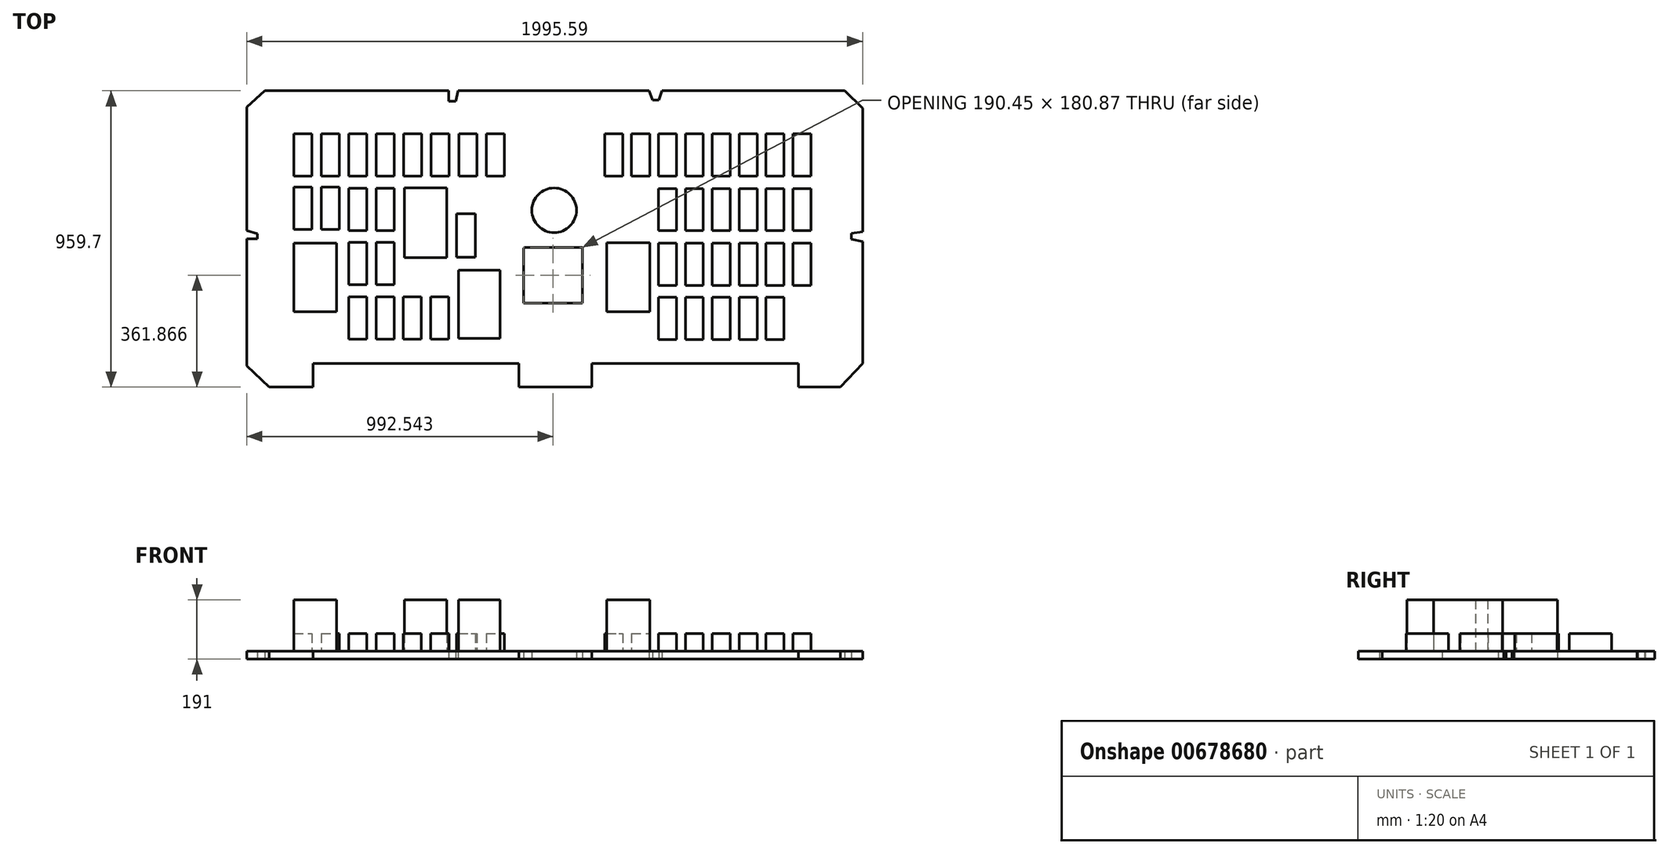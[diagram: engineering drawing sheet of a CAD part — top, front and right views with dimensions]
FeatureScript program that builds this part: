
annotation { "Feature Type Name" : "Feature", "Feature Type Description" : "" }
export const myFeature = defineFeature(function(context is Context, id is Id, definition is map)
    precondition{}
    {
        {
            var Q0;
            Q0=qCreatedBy(makeId("Top.planeOp"),FACE);
            var sketch = newSketch(context, id + "F0", { "sketchPlane" : qUnion([Q0])});
            skLineSegment(sketch, "E0.bottom", {"start": v(-887.12, 318.46) * mm, "end": v(-290.84, 318.46) * mm});
            skLineSegment(sketch, "E0.top", {"start": v(-872.01, -641.24) * mm, "end": v(-729.99, -641.24) * mm});
            skLineSegment(sketch, "E0.left", {"start": v(-945.57, 265.32) * mm, "end": v(-945.57, -134.43) * mm});
            skLineSegment(sketch, "E0.right", {"start": v(1050.02, 261.3) * mm, "end": v(1050.02, -138.6) * mm});
            skLineSegment(sketch, "E1.bottom", {"start": v(-792.44, 178.7) * mm, "end": v(-734.02, 178.7) * mm});
            skLineSegment(sketch, "E1.top", {"start": v(-792.44, 41.72) * mm, "end": v(-734.02, 41.72) * mm});
            skLineSegment(sketch, "E1.left", {"start": v(-792.44, 178.7) * mm, "end": v(-792.44, 41.72) * mm});
            skLineSegment(sketch, "E1.right", {"start": v(-734.02, 178.7) * mm, "end": v(-734.02, 41.72) * mm});
            skLineSegment(sketch, "E2.1.0.0", {"start": v(-703.44, 178.7) * mm, "end": v(-645.02, 178.7) * mm});
            skLineSegment(sketch, "E2.1.0.1", {"start": v(-703.44, 41.72) * mm, "end": v(-645.02, 41.72) * mm});
            skLineSegment(sketch, "E2.1.0.2", {"start": v(-703.44, 178.7) * mm, "end": v(-703.44, 41.72) * mm});
            skLineSegment(sketch, "E2.1.0.3", {"start": v(-645.02, 178.7) * mm, "end": v(-645.02, 41.72) * mm});
            skLineSegment(sketch, "E2.2.0.0", {"start": v(-614.44, 178.7) * mm, "end": v(-556.02, 178.7) * mm});
            skLineSegment(sketch, "E2.2.0.1", {"start": v(-614.44, 41.72) * mm, "end": v(-556.02, 41.72) * mm});
            skLineSegment(sketch, "E2.2.0.2", {"start": v(-614.44, 178.7) * mm, "end": v(-614.44, 41.72) * mm});
            skLineSegment(sketch, "E2.2.0.3", {"start": v(-556.02, 178.7) * mm, "end": v(-556.02, 41.72) * mm});
            skLineSegment(sketch, "E2.3.0.0", {"start": v(-525.44, 178.7) * mm, "end": v(-467.02, 178.7) * mm});
            skLineSegment(sketch, "E2.3.0.1", {"start": v(-525.44, 41.72) * mm, "end": v(-467.02, 41.72) * mm});
            skLineSegment(sketch, "E2.3.0.2", {"start": v(-525.44, 178.7) * mm, "end": v(-525.44, 41.72) * mm});
            skLineSegment(sketch, "E2.3.0.3", {"start": v(-467.02, 178.7) * mm, "end": v(-467.02, 41.72) * mm});
            skLineSegment(sketch, "E2.4.0.0", {"start": v(-436.44, 178.7) * mm, "end": v(-378.02, 178.7) * mm});
            skLineSegment(sketch, "E2.4.0.1", {"start": v(-436.44, 41.72) * mm, "end": v(-378.02, 41.72) * mm});
            skLineSegment(sketch, "E2.4.0.2", {"start": v(-436.44, 178.7) * mm, "end": v(-436.44, 41.72) * mm});
            skLineSegment(sketch, "E2.4.0.3", {"start": v(-378.02, 178.7) * mm, "end": v(-378.02, 41.72) * mm});
            skLineSegment(sketch, "E2.5.0.0", {"start": v(-347.44, 178.7) * mm, "end": v(-289.02, 178.7) * mm});
            skLineSegment(sketch, "E2.5.0.1", {"start": v(-347.44, 41.72) * mm, "end": v(-289.02, 41.72) * mm});
            skLineSegment(sketch, "E2.5.0.2", {"start": v(-347.44, 178.7) * mm, "end": v(-347.44, 41.72) * mm});
            skLineSegment(sketch, "E2.5.0.3", {"start": v(-289.02, 178.7) * mm, "end": v(-289.02, 41.72) * mm});
            skLineSegment(sketch, "E2.6.0.0", {"start": v(-258.44, 178.7) * mm, "end": v(-200.02, 178.7) * mm});
            skLineSegment(sketch, "E2.6.0.1", {"start": v(-258.44, 41.72) * mm, "end": v(-200.02, 41.72) * mm});
            skLineSegment(sketch, "E2.6.0.2", {"start": v(-258.44, 178.7) * mm, "end": v(-258.44, 41.72) * mm});
            skLineSegment(sketch, "E2.6.0.3", {"start": v(-200.02, 178.7) * mm, "end": v(-200.02, 41.72) * mm});
            skLineSegment(sketch, "E2.7.0.0", {"start": v(-169.44, 178.7) * mm, "end": v(-111.02, 178.7) * mm});
            skLineSegment(sketch, "E2.7.0.1", {"start": v(-169.44, 41.72) * mm, "end": v(-111.02, 41.72) * mm});
            skLineSegment(sketch, "E2.7.0.2", {"start": v(-169.44, 178.7) * mm, "end": v(-169.44, 41.72) * mm});
            skLineSegment(sketch, "E2.7.0.3", {"start": v(-111.02, 178.7) * mm, "end": v(-111.02, 41.72) * mm});
            skLineSegment(sketch, "E2.direction1", {"start": v(-792.44, 41.72) * mm, "end": v(-703.44, 41.72) * mm, "construction": true});
            skPoint(sketch, "E3", {"position": v(-945.57, 265.32) * mm});
            skPoint(sketch, "E4", {"position": v(-887.12, 318.46) * mm});
            skPoint(sketch, "E5", {"position": v(-290.84, 318.46) * mm});
            skPoint(sketch, "E6", {"position": v(-260.62, 318.46) * mm});
            skPoint(sketch, "E7", {"position": v(357.82, 318.46) * mm});
            skPoint(sketch, "E8", {"position": v(400.12, 318.46) * mm});
            skPoint(sketch, "E9", {"position": v(992.37, 318.46) * mm});
            skPoint(sketch, "E10", {"position": v(1050.02, 261.3) * mm});
            skPoint(sketch, "E11", {"position": v(1050.02, -564.63) * mm});
            skPoint(sketch, "E12", {"position": v(978.27, -641.24) * mm});
            skPoint(sketch, "E13", {"position": v(841.29, -641.24) * mm});
            skPoint(sketch, "E14", {"position": v(172.49, -641.24) * mm});
            skPoint(sketch, "E15", {"position": v(-63.2, -641.24) * mm});
            skPoint(sketch, "E16", {"position": v(-729.99, -641.24) * mm});
            skLineSegment(sketch, "E17", {"start": v(-945.57, 265.32) * mm, "end": v(-887.12, 318.46) * mm});
            skLineSegment(sketch, "E18", {"start": v(-290.84, 318.46) * mm, "end": v(-290.84, 284.99) * mm});
            skLineSegment(sketch, "E19", {"start": v(-290.84, 284.99) * mm, "end": v(-268.29, 284.99) * mm});
            skLineSegment(sketch, "E20", {"start": v(-268.29, 284.99) * mm, "end": v(-260.62, 318.46) * mm});
            skLineSegment(sketch, "E21", {"start": v(357.82, 318.46) * mm, "end": v(369.4, 287.8) * mm});
            skLineSegment(sketch, "E22", {"start": v(369.4, 287.8) * mm, "end": v(389.55, 287.8) * mm});
            skLineSegment(sketch, "E23", {"start": v(389.55, 287.8) * mm, "end": v(400.12, 318.46) * mm});
            skLineSegment(sketch, "E24", {"start": v(992.37, 318.46) * mm, "end": v(1050.02, 261.3) * mm});
            skLineSegment(sketch, "E25", {"start": v(1050.02, -564.63) * mm, "end": v(978.27, -641.24) * mm});
            skLineSegment(sketch, "E26", {"start": v(841.29, -641.24) * mm, "end": v(841.29, -564.63) * mm});
            skLineSegment(sketch, "E27", {"start": v(841.29, -564.63) * mm, "end": v(172.49, -564.63) * mm});
            skLineSegment(sketch, "E28", {"start": v(172.49, -564.63) * mm, "end": v(172.49, -641.24) * mm});
            skLineSegment(sketch, "E29", {"start": v(-63.2, -641.24) * mm, "end": v(-63.2, -564.63) * mm});
            skLineSegment(sketch, "E30", {"start": v(-63.2, -564.63) * mm, "end": v(-729.99, -564.63) * mm});
            skLineSegment(sketch, "E31", {"start": v(-729.99, -564.63) * mm, "end": v(-729.99, -641.24) * mm});
            skPoint(sketch, "E32", {"position": v(-872.01, -641.24) * mm});
            skPoint(sketch, "E33", {"position": v(-945.57, -572.57) * mm});
            skPoint(sketch, "E34", {"position": v(-945.57, -161.39) * mm});
            skPoint(sketch, "E35", {"position": v(-945.57, -134.43) * mm});
            skLineSegment(sketch, "E36", {"start": v(-945.57, -134.43) * mm, "end": v(-910.29, -144.5) * mm});
            skLineSegment(sketch, "E37", {"start": v(-910.29, -144.5) * mm, "end": v(-910.29, -161.62) * mm});
            skLineSegment(sketch, "E38", {"start": v(-910.29, -161.62) * mm, "end": v(-945.57, -161.39) * mm});
            skLineSegment(sketch, "E39", {"start": v(-945.57, -572.57) * mm, "end": v(-872.01, -641.24) * mm});
            skPoint(sketch, "E40.orphan", {"position": v(-945.57, -641.24) * mm});
            skLineSegment(sketch, "E41.trimOffspring", {"start": v(-63.2, -641.24) * mm, "end": v(172.49, -641.24) * mm});
            skLineSegment(sketch, "E42.trimOffspring", {"start": v(841.29, -641.24) * mm, "end": v(978.27, -641.24) * mm});
            skLineSegment(sketch, "E43", {"start": v(1050.02, -138.6) * mm, "end": v(1013.26, -143.68) * mm});
            skLineSegment(sketch, "E44", {"start": v(1013.26, -143.68) * mm, "end": v(1013.26, -163.16) * mm});
            skLineSegment(sketch, "E45", {"start": v(1013.26, -163.16) * mm, "end": v(1050.02, -170.78) * mm});
            skLineSegment(sketch, "E46.trimOffspring", {"start": v(1050.02, -170.78) * mm, "end": v(1050.02, -564.63) * mm});
            skLineSegment(sketch, "E47.trimOffspring", {"start": v(-945.57, -161.39) * mm, "end": v(-945.57, -572.57) * mm});
            skPoint(sketch, "E48.orphan", {"position": v(-945.57, 318.46) * mm});
            skLineSegment(sketch, "E49.trimOffspring", {"start": v(-260.62, 318.46) * mm, "end": v(357.82, 318.46) * mm});
            skLineSegment(sketch, "E50.trimOffspring", {"start": v(400.12, 318.46) * mm, "end": v(992.37, 318.46) * mm});
            skLineSegment(sketch, "E51.0.1.0", {"start": v(-792.44, 6.7) * mm, "end": v(-792.44, -130.28) * mm});
            skLineSegment(sketch, "E51.0.1.1", {"start": v(-703.44, 6.7) * mm, "end": v(-645.02, 6.7) * mm});
            skLineSegment(sketch, "E51.0.1.2", {"start": v(-792.44, -130.28) * mm, "end": v(-734.02, -130.28) * mm});
            skLineSegment(sketch, "E51.0.1.4", {"start": v(-792.44, 6.7) * mm, "end": v(-734.02, 6.7) * mm});
            skLineSegment(sketch, "E51.0.1.5", {"start": v(-734.02, 6.7) * mm, "end": v(-734.02, -130.28) * mm});
            skLineSegment(sketch, "E51.0.1.10", {"start": v(-703.44, -130.28) * mm, "end": v(-645.02, -130.28) * mm});
            skLineSegment(sketch, "E51.0.1.11", {"start": v(-645.02, 6.7) * mm, "end": v(-645.02, -130.28) * mm});
            skLineSegment(sketch, "E51.0.1.12", {"start": v(-703.44, 6.7) * mm, "end": v(-703.44, -130.28) * mm});
            skLineSegment(sketch, "E51.0.1.16", {"start": v(-792.44, -130.28) * mm, "end": v(-703.44, -130.28) * mm, "construction": true});
            skLineSegment(sketch, "E51.direction1", {"start": v(-792.44, 41.72) * mm, "end": v(-767.44, 41.72) * mm, "construction": true});
            skLineSegment(sketch, "E51.direction2", {"start": v(-792.44, 41.72) * mm, "end": v(-792.44, -130.28) * mm, "construction": true});
            skLineSegment(sketch, "E52.bottom", {"start": v(-434.49, 3.44) * mm, "end": v(-297.5, 3.44) * mm});
            skLineSegment(sketch, "E52.top", {"start": v(-434.49, -222.18) * mm, "end": v(-297.5, -222.18) * mm});
            skLineSegment(sketch, "E52.left", {"start": v(-434.49, 3.44) * mm, "end": v(-434.49, -222.18) * mm});
            skLineSegment(sketch, "E52.right", {"start": v(-297.5, 3.44) * mm, "end": v(-297.5, -222.18) * mm});
            skLineSegment(sketch, "E53.bottom", {"start": v(-793.06, -175.84) * mm, "end": v(-654.06, -175.84) * mm});
            skLineSegment(sketch, "E53.top", {"start": v(-793.06, -397.43) * mm, "end": v(-654.06, -397.43) * mm});
            skLineSegment(sketch, "E53.left", {"start": v(-793.06, -175.84) * mm, "end": v(-793.06, -397.43) * mm});
            skLineSegment(sketch, "E53.right", {"start": v(-654.06, -175.84) * mm, "end": v(-654.06, -397.43) * mm});
            skLineSegment(sketch, "E54.bottom", {"start": v(-259.23, -262.47) * mm, "end": v(-124.26, -262.47) * mm});
            skLineSegment(sketch, "E54.top", {"start": v(-259.23, -484.06) * mm, "end": v(-124.26, -484.06) * mm});
            skLineSegment(sketch, "E54.left", {"start": v(-259.23, -262.47) * mm, "end": v(-259.23, -484.06) * mm});
            skLineSegment(sketch, "E54.right", {"start": v(-124.26, -262.47) * mm, "end": v(-124.26, -484.06) * mm});
            skLineSegment(sketch, "E55.0.1.0", {"start": v(-525.44, -134.28) * mm, "end": v(-467.02, -134.28) * mm});
            skLineSegment(sketch, "E55.0.1.1", {"start": v(-525.44, 2.7) * mm, "end": v(-525.44, -134.28) * mm});
            skLineSegment(sketch, "E55.0.1.2", {"start": v(-525.44, 2.7) * mm, "end": v(-467.02, 2.7) * mm});
            skLineSegment(sketch, "E55.0.1.3", {"start": v(-614.44, -134.28) * mm, "end": v(-556.02, -134.28) * mm});
            skLineSegment(sketch, "E55.0.1.4", {"start": v(-467.02, 2.7) * mm, "end": v(-467.02, -134.28) * mm});
            skLineSegment(sketch, "E55.0.1.5", {"start": v(-556.02, 2.7) * mm, "end": v(-556.02, -134.28) * mm});
            skLineSegment(sketch, "E55.0.1.6", {"start": v(-614.44, 2.7) * mm, "end": v(-556.02, 2.7) * mm});
            skLineSegment(sketch, "E55.0.1.7", {"start": v(-614.44, 2.7) * mm, "end": v(-614.44, -134.28) * mm});
            skLineSegment(sketch, "E55.0.2.0", {"start": v(-525.44, -310.28) * mm, "end": v(-467.02, -310.28) * mm});
            skLineSegment(sketch, "E55.0.2.1", {"start": v(-525.44, -173.3) * mm, "end": v(-525.44, -310.28) * mm});
            skLineSegment(sketch, "E55.0.2.2", {"start": v(-525.44, -173.3) * mm, "end": v(-467.02, -173.3) * mm});
            skLineSegment(sketch, "E55.0.2.3", {"start": v(-614.44, -310.28) * mm, "end": v(-556.02, -310.28) * mm});
            skLineSegment(sketch, "E55.0.2.4", {"start": v(-467.02, -173.3) * mm, "end": v(-467.02, -310.28) * mm});
            skLineSegment(sketch, "E55.0.2.5", {"start": v(-556.02, -173.3) * mm, "end": v(-556.02, -310.28) * mm});
            skLineSegment(sketch, "E55.0.2.6", {"start": v(-614.44, -173.3) * mm, "end": v(-556.02, -173.3) * mm});
            skLineSegment(sketch, "E55.0.2.7", {"start": v(-614.44, -173.3) * mm, "end": v(-614.44, -310.28) * mm});
            skLineSegment(sketch, "E55.0.3.0", {"start": v(-525.44, -486.28) * mm, "end": v(-467.02, -486.28) * mm});
            skLineSegment(sketch, "E55.0.3.1", {"start": v(-525.44, -349.3) * mm, "end": v(-525.44, -486.28) * mm});
            skLineSegment(sketch, "E55.0.3.2", {"start": v(-525.44, -349.3) * mm, "end": v(-467.02, -349.3) * mm});
            skLineSegment(sketch, "E55.0.3.3", {"start": v(-614.44, -486.28) * mm, "end": v(-556.02, -486.28) * mm});
            skLineSegment(sketch, "E55.0.3.4", {"start": v(-467.02, -349.3) * mm, "end": v(-467.02, -486.28) * mm});
            skLineSegment(sketch, "E55.0.3.5", {"start": v(-556.02, -349.3) * mm, "end": v(-556.02, -486.28) * mm});
            skLineSegment(sketch, "E55.0.3.6", {"start": v(-614.44, -349.3) * mm, "end": v(-556.02, -349.3) * mm});
            skLineSegment(sketch, "E55.0.3.7", {"start": v(-614.44, -349.3) * mm, "end": v(-614.44, -486.28) * mm});
            skLineSegment(sketch, "E55.direction1", {"start": v(-614.44, 41.72) * mm, "end": v(-589.44, 41.72) * mm, "construction": true});
            skLineSegment(sketch, "E55.direction2", {"start": v(-614.44, 41.72) * mm, "end": v(-614.44, -134.28) * mm, "construction": true});
            skLineSegment(sketch, "E56.1.0.0", {"start": v(-438.44, -486.28) * mm, "end": v(-380.02, -486.28) * mm});
            skLineSegment(sketch, "E56.1.0.1", {"start": v(-349.44, -486.28) * mm, "end": v(-291.02, -486.28) * mm});
            skLineSegment(sketch, "E56.1.0.2", {"start": v(-349.44, -349.3) * mm, "end": v(-291.02, -349.3) * mm});
            skLineSegment(sketch, "E56.1.0.3", {"start": v(-349.44, -349.3) * mm, "end": v(-349.44, -486.28) * mm});
            skLineSegment(sketch, "E56.1.0.4", {"start": v(-438.44, -349.3) * mm, "end": v(-438.44, -486.28) * mm});
            skLineSegment(sketch, "E56.1.0.5", {"start": v(-291.02, -349.3) * mm, "end": v(-291.02, -486.28) * mm});
            skLineSegment(sketch, "E56.1.0.6", {"start": v(-380.02, -349.3) * mm, "end": v(-380.02, -486.28) * mm});
            skLineSegment(sketch, "E56.1.0.7", {"start": v(-438.44, -349.3) * mm, "end": v(-380.02, -349.3) * mm});
            skLineSegment(sketch, "E56.direction1", {"start": v(-614.44, -486.28) * mm, "end": v(-438.44, -486.28) * mm, "construction": true});
            skLineSegment(sketch, "E57.bottom", {"start": v(221.15, -174.55) * mm, "end": v(360.1, -174.55) * mm});
            skLineSegment(sketch, "E57.top", {"start": v(221.15, -397.34) * mm, "end": v(360.1, -397.34) * mm});
            skLineSegment(sketch, "E57.left", {"start": v(221.15, -174.55) * mm, "end": v(221.15, -397.34) * mm});
            skLineSegment(sketch, "E57.right", {"start": v(360.1, -174.55) * mm, "end": v(360.1, -397.34) * mm});
            skLineSegment(sketch, "E58.1.0.0", {"start": v(272.98, 178.7) * mm, "end": v(272.98, 41.72) * mm});
            skLineSegment(sketch, "E58.1.0.1", {"start": v(214.56, 178.7) * mm, "end": v(214.56, 41.72) * mm});
            skLineSegment(sketch, "E58.1.0.2", {"start": v(214.56, 41.72) * mm, "end": v(272.98, 41.72) * mm});
            skLineSegment(sketch, "E58.1.0.3", {"start": v(214.56, 178.7) * mm, "end": v(272.98, 178.7) * mm});
            skLineSegment(sketch, "E58.direction1", {"start": v(-169.44, 41.72) * mm, "end": v(214.56, 41.72) * mm, "construction": true});
            skLineSegment(sketch, "E59.1.0.0", {"start": v(301.56, 178.7) * mm, "end": v(301.56, 41.72) * mm});
            skLineSegment(sketch, "E59.1.0.1", {"start": v(359.98, 178.7) * mm, "end": v(359.98, 41.72) * mm});
            skLineSegment(sketch, "E59.1.0.2", {"start": v(301.56, 178.7) * mm, "end": v(359.98, 178.7) * mm});
            skLineSegment(sketch, "E59.1.0.3", {"start": v(301.56, 41.72) * mm, "end": v(359.98, 41.72) * mm});
            skLineSegment(sketch, "E59.2.0.0", {"start": v(388.56, 178.7) * mm, "end": v(388.56, 41.72) * mm});
            skLineSegment(sketch, "E59.2.0.1", {"start": v(446.98, 178.7) * mm, "end": v(446.98, 41.72) * mm});
            skLineSegment(sketch, "E59.2.0.2", {"start": v(388.56, 178.7) * mm, "end": v(446.98, 178.7) * mm});
            skLineSegment(sketch, "E59.2.0.3", {"start": v(388.56, 41.72) * mm, "end": v(446.98, 41.72) * mm});
            skLineSegment(sketch, "E59.3.0.0", {"start": v(475.56, 178.7) * mm, "end": v(475.56, 41.72) * mm});
            skLineSegment(sketch, "E59.3.0.1", {"start": v(533.98, 178.7) * mm, "end": v(533.98, 41.72) * mm});
            skLineSegment(sketch, "E59.3.0.2", {"start": v(475.56, 178.7) * mm, "end": v(533.98, 178.7) * mm});
            skLineSegment(sketch, "E59.3.0.3", {"start": v(475.56, 41.72) * mm, "end": v(533.98, 41.72) * mm});
            skLineSegment(sketch, "E59.4.0.0", {"start": v(562.56, 178.7) * mm, "end": v(562.56, 41.72) * mm});
            skLineSegment(sketch, "E59.4.0.1", {"start": v(620.98, 178.7) * mm, "end": v(620.98, 41.72) * mm});
            skLineSegment(sketch, "E59.4.0.2", {"start": v(562.56, 178.7) * mm, "end": v(620.98, 178.7) * mm});
            skLineSegment(sketch, "E59.4.0.3", {"start": v(562.56, 41.72) * mm, "end": v(620.98, 41.72) * mm});
            skLineSegment(sketch, "E59.5.0.0", {"start": v(649.56, 178.7) * mm, "end": v(649.56, 41.72) * mm});
            skLineSegment(sketch, "E59.5.0.1", {"start": v(707.98, 178.7) * mm, "end": v(707.98, 41.72) * mm});
            skLineSegment(sketch, "E59.5.0.2", {"start": v(649.56, 178.7) * mm, "end": v(707.98, 178.7) * mm});
            skLineSegment(sketch, "E59.5.0.3", {"start": v(649.56, 41.72) * mm, "end": v(707.98, 41.72) * mm});
            skLineSegment(sketch, "E59.6.0.0", {"start": v(736.56, 178.7) * mm, "end": v(736.56, 41.72) * mm});
            skLineSegment(sketch, "E59.6.0.1", {"start": v(794.98, 178.7) * mm, "end": v(794.98, 41.72) * mm});
            skLineSegment(sketch, "E59.6.0.2", {"start": v(736.56, 178.7) * mm, "end": v(794.98, 178.7) * mm});
            skLineSegment(sketch, "E59.6.0.3", {"start": v(736.56, 41.72) * mm, "end": v(794.98, 41.72) * mm});
            skLineSegment(sketch, "E59.7.0.0", {"start": v(823.56, 178.7) * mm, "end": v(823.56, 41.72) * mm});
            skLineSegment(sketch, "E59.7.0.1", {"start": v(881.98, 178.7) * mm, "end": v(881.98, 41.72) * mm});
            skLineSegment(sketch, "E59.7.0.2", {"start": v(823.56, 178.7) * mm, "end": v(881.98, 178.7) * mm});
            skLineSegment(sketch, "E59.7.0.3", {"start": v(823.56, 41.72) * mm, "end": v(881.98, 41.72) * mm});
            skLineSegment(sketch, "E59.direction1", {"start": v(214.56, 41.72) * mm, "end": v(301.56, 41.72) * mm, "construction": true});
            skLineSegment(sketch, "E60.0.1.0", {"start": v(823.56, -135.28) * mm, "end": v(881.98, -135.28) * mm});
            skLineSegment(sketch, "E60.0.1.1", {"start": v(649.56, 1.7) * mm, "end": v(649.56, -135.28) * mm});
            skLineSegment(sketch, "E60.0.1.2", {"start": v(562.56, -135.28) * mm, "end": v(620.98, -135.28) * mm});
            skLineSegment(sketch, "E60.0.1.3", {"start": v(562.56, 1.7) * mm, "end": v(620.98, 1.7) * mm});
            skLineSegment(sketch, "E60.0.1.4", {"start": v(707.98, 1.7) * mm, "end": v(707.98, -135.28) * mm});
            skLineSegment(sketch, "E60.0.1.5", {"start": v(881.98, 1.7) * mm, "end": v(881.98, -135.28) * mm});
            skLineSegment(sketch, "E60.0.1.6", {"start": v(620.98, 1.7) * mm, "end": v(620.98, -135.28) * mm});
            skLineSegment(sketch, "E60.0.1.7", {"start": v(649.56, 1.7) * mm, "end": v(707.98, 1.7) * mm});
            skLineSegment(sketch, "E60.0.1.8", {"start": v(475.56, -135.28) * mm, "end": v(533.98, -135.28) * mm});
            skLineSegment(sketch, "E60.0.1.9", {"start": v(388.56, -135.28) * mm, "end": v(446.98, -135.28) * mm});
            skLineSegment(sketch, "E60.0.1.10", {"start": v(562.56, 1.7) * mm, "end": v(562.56, -135.28) * mm});
            skLineSegment(sketch, "E60.0.1.11", {"start": v(736.56, -135.28) * mm, "end": v(794.98, -135.28) * mm});
            skLineSegment(sketch, "E60.0.1.12", {"start": v(533.98, 1.7) * mm, "end": v(533.98, -135.28) * mm});
            skLineSegment(sketch, "E60.0.1.13", {"start": v(736.56, 1.7) * mm, "end": v(794.98, 1.7) * mm});
            skLineSegment(sketch, "E60.0.1.14", {"start": v(649.56, -135.28) * mm, "end": v(707.98, -135.28) * mm});
            skLineSegment(sketch, "E60.0.1.15", {"start": v(475.56, 1.7) * mm, "end": v(533.98, 1.7) * mm});
            skLineSegment(sketch, "E60.0.1.16", {"start": v(823.56, 1.7) * mm, "end": v(881.98, 1.7) * mm});
            skLineSegment(sketch, "E60.0.1.17", {"start": v(446.98, 1.7) * mm, "end": v(446.98, -135.28) * mm});
            skLineSegment(sketch, "E60.0.1.18", {"start": v(794.98, 1.7) * mm, "end": v(794.98, -135.28) * mm});
            skLineSegment(sketch, "E60.0.1.19", {"start": v(475.56, 1.7) * mm, "end": v(475.56, -135.28) * mm});
            skLineSegment(sketch, "E60.0.1.20", {"start": v(736.56, 1.7) * mm, "end": v(736.56, -135.28) * mm});
            skLineSegment(sketch, "E60.0.1.21", {"start": v(388.56, 1.7) * mm, "end": v(388.56, -135.28) * mm});
            skLineSegment(sketch, "E60.0.1.22", {"start": v(388.56, 1.7) * mm, "end": v(446.98, 1.7) * mm});
            skLineSegment(sketch, "E60.0.1.23", {"start": v(823.56, 1.7) * mm, "end": v(823.56, -135.28) * mm});
            skLineSegment(sketch, "E60.0.2.0", {"start": v(823.56, -312.28) * mm, "end": v(881.98, -312.28) * mm});
            skLineSegment(sketch, "E60.0.2.1", {"start": v(649.56, -175.3) * mm, "end": v(649.56, -312.28) * mm});
            skLineSegment(sketch, "E60.0.2.2", {"start": v(562.56, -312.28) * mm, "end": v(620.98, -312.28) * mm});
            skLineSegment(sketch, "E60.0.2.3", {"start": v(562.56, -175.3) * mm, "end": v(620.98, -175.3) * mm});
            skLineSegment(sketch, "E60.0.2.4", {"start": v(707.98, -175.3) * mm, "end": v(707.98, -312.28) * mm});
            skLineSegment(sketch, "E60.0.2.5", {"start": v(881.98, -175.3) * mm, "end": v(881.98, -312.28) * mm});
            skLineSegment(sketch, "E60.0.2.6", {"start": v(620.98, -175.3) * mm, "end": v(620.98, -312.28) * mm});
            skLineSegment(sketch, "E60.0.2.7", {"start": v(649.56, -175.3) * mm, "end": v(707.98, -175.3) * mm});
            skLineSegment(sketch, "E60.0.2.8", {"start": v(475.56, -312.28) * mm, "end": v(533.98, -312.28) * mm});
            skLineSegment(sketch, "E60.0.2.9", {"start": v(388.56, -312.28) * mm, "end": v(446.98, -312.28) * mm});
            skLineSegment(sketch, "E60.0.2.10", {"start": v(562.56, -175.3) * mm, "end": v(562.56, -312.28) * mm});
            skLineSegment(sketch, "E60.0.2.11", {"start": v(736.56, -312.28) * mm, "end": v(794.98, -312.28) * mm});
            skLineSegment(sketch, "E60.0.2.12", {"start": v(533.98, -175.3) * mm, "end": v(533.98, -312.28) * mm});
            skLineSegment(sketch, "E60.0.2.13", {"start": v(736.56, -175.3) * mm, "end": v(794.98, -175.3) * mm});
            skLineSegment(sketch, "E60.0.2.14", {"start": v(649.56, -312.28) * mm, "end": v(707.98, -312.28) * mm});
            skLineSegment(sketch, "E60.0.2.15", {"start": v(475.56, -175.3) * mm, "end": v(533.98, -175.3) * mm});
            skLineSegment(sketch, "E60.0.2.16", {"start": v(823.56, -175.3) * mm, "end": v(881.98, -175.3) * mm});
            skLineSegment(sketch, "E60.0.2.17", {"start": v(446.98, -175.3) * mm, "end": v(446.98, -312.28) * mm});
            skLineSegment(sketch, "E60.0.2.18", {"start": v(794.98, -175.3) * mm, "end": v(794.98, -312.28) * mm});
            skLineSegment(sketch, "E60.0.2.19", {"start": v(475.56, -175.3) * mm, "end": v(475.56, -312.28) * mm});
            skLineSegment(sketch, "E60.0.2.20", {"start": v(736.56, -175.3) * mm, "end": v(736.56, -312.28) * mm});
            skLineSegment(sketch, "E60.0.2.21", {"start": v(388.56, -175.3) * mm, "end": v(388.56, -312.28) * mm});
            skLineSegment(sketch, "E60.0.2.22", {"start": v(388.56, -175.3) * mm, "end": v(446.98, -175.3) * mm});
            skLineSegment(sketch, "E60.0.2.23", {"start": v(823.56, -175.3) * mm, "end": v(823.56, -312.28) * mm});
            skLineSegment(sketch, "E60.direction1", {"start": v(388.56, 41.72) * mm, "end": v(413.56, 41.72) * mm, "construction": true});
            skLineSegment(sketch, "E60.direction2", {"start": v(388.56, 41.72) * mm, "end": v(388.56, -135.28) * mm, "construction": true});
            skLineSegment(sketch, "E61.0.1.0", {"start": v(475.56, -487.28) * mm, "end": v(533.98, -487.28) * mm});
            skLineSegment(sketch, "E61.0.1.1", {"start": v(649.56, -350.3) * mm, "end": v(707.98, -350.3) * mm});
            skLineSegment(sketch, "E61.0.1.2", {"start": v(649.56, -487.28) * mm, "end": v(707.98, -487.28) * mm});
            skLineSegment(sketch, "E61.0.1.3", {"start": v(562.56, -487.28) * mm, "end": v(620.98, -487.28) * mm});
            skLineSegment(sketch, "E61.0.1.4", {"start": v(388.56, -487.28) * mm, "end": v(446.98, -487.28) * mm});
            skLineSegment(sketch, "E61.0.1.5", {"start": v(794.98, -350.3) * mm, "end": v(794.98, -487.28) * mm});
            skLineSegment(sketch, "E61.0.1.6", {"start": v(475.56, -350.3) * mm, "end": v(533.98, -350.3) * mm});
            skLineSegment(sketch, "E61.0.1.7", {"start": v(446.98, -350.3) * mm, "end": v(446.98, -487.28) * mm});
            skLineSegment(sketch, "E61.0.1.8", {"start": v(649.56, -350.3) * mm, "end": v(649.56, -487.28) * mm});
            skLineSegment(sketch, "E61.0.1.9", {"start": v(620.98, -350.3) * mm, "end": v(620.98, -487.28) * mm});
            skLineSegment(sketch, "E61.0.1.10", {"start": v(388.56, -350.3) * mm, "end": v(446.98, -350.3) * mm});
            skLineSegment(sketch, "E61.0.1.11", {"start": v(736.56, -350.3) * mm, "end": v(794.98, -350.3) * mm});
            skLineSegment(sketch, "E61.0.1.12", {"start": v(533.98, -350.3) * mm, "end": v(533.98, -487.28) * mm});
            skLineSegment(sketch, "E61.0.1.13", {"start": v(736.56, -487.28) * mm, "end": v(794.98, -487.28) * mm});
            skLineSegment(sketch, "E61.0.1.14", {"start": v(562.56, -350.3) * mm, "end": v(562.56, -487.28) * mm});
            skLineSegment(sketch, "E61.0.1.15", {"start": v(475.56, -350.3) * mm, "end": v(475.56, -487.28) * mm});
            skLineSegment(sketch, "E61.0.1.16", {"start": v(562.56, -350.3) * mm, "end": v(620.98, -350.3) * mm});
            skLineSegment(sketch, "E61.0.1.17", {"start": v(736.56, -350.3) * mm, "end": v(736.56, -487.28) * mm});
            skLineSegment(sketch, "E61.0.1.18", {"start": v(707.98, -350.3) * mm, "end": v(707.98, -487.28) * mm});
            skLineSegment(sketch, "E61.0.1.19", {"start": v(388.56, -350.3) * mm, "end": v(388.56, -487.28) * mm});
            skLineSegment(sketch, "E61.direction1", {"start": v(388.56, -312.28) * mm, "end": v(413.56, -312.28) * mm, "construction": true});
            skLineSegment(sketch, "E61.direction2", {"start": v(388.56, -312.28) * mm, "end": v(388.56, -487.28) * mm, "construction": true});
            skLineSegment(sketch, "E62.bottom", {"start": v(-264.94, -80.47) * mm, "end": v(-205.11, -80.47) * mm});
            skLineSegment(sketch, "E62.top", {"start": v(-264.94, -221.49) * mm, "end": v(-205.11, -221.49) * mm});
            skLineSegment(sketch, "E62.left", {"start": v(-264.94, -80.47) * mm, "end": v(-264.94, -221.49) * mm});
            skLineSegment(sketch, "E62.right", {"start": v(-205.11, -80.47) * mm, "end": v(-205.11, -221.49) * mm});
            skLineSegment(sketch, "E63.bottom", {"start": v(-43.25, -188.94) * mm, "end": v(142.2, -188.94) * mm});
            skLineSegment(sketch, "E63.top", {"start": v(-48.25, -369.8) * mm, "end": v(142.2, -369.8) * mm});
            skLineSegment(sketch, "E63.left", {"start": v(-48.25, -193.94) * mm, "end": v(-48.25, -369.8) * mm});
            skLineSegment(sketch, "E63.right", {"start": v(142.2, -188.94) * mm, "end": v(142.2, -369.8) * mm});
            skPoint(sketch, "E64.visualSharp", {"position": v(-48.25, -188.94) * mm});
            skArc(sketch, "E64.filletArc", {"start": v(-43.25, -188.94) * mm, "mid": v(-46.79, -190.4) * mm, "end": v(-48.25, -193.94) * mm});
            skCircle(sketch, "E65", {"center": v(50.63, -68.9) * mm, "radius": 72.28 * mm});
            skSolve(sketch);
        }
        {
            var Q0;
            Q0=makeQuery(id+"F0.imprint","IMPRINT",FACE,{"disambiguationData":[TD([[makeQuery(id+"F0.imprint","IMPRINT",EDGE,{"derivedFrom":sQuery(id+"F0.wireOp",EDGE,"E0.bottom")}),-1.0]])]});
            extrude(context, id + "F1", {"entities" : qUnion([Q0]), "depth" : 25 * mm, "offsetDistance" : 25 * mm});
        }
        {
            var Q0;
            Q0=makeQuery(id+"F0.imprint","IMPRINT",FACE,{"disambiguationData":[TD([[makeQuery(id+"F0.imprint","IMPRINT",EDGE,{"derivedFrom":sQuery(id+"F0.wireOp",EDGE,"E1.bottom")}),-1.0]])]});
            var Q1;
            Q1=makeQuery(id+"F0.imprint","IMPRINT",FACE,{"disambiguationData":[TD([[makeQuery(id+"F0.imprint","IMPRINT",EDGE,{"derivedFrom":sQuery(id+"F0.wireOp",EDGE,"E2.1.0.0")}),-1.0]])]});
            var Q2;
            Q2=makeQuery(id+"F0.imprint","IMPRINT",FACE,{"disambiguationData":[TD([[makeQuery(id+"F0.imprint","IMPRINT",EDGE,{"derivedFrom":sQuery(id+"F0.wireOp",EDGE,"E2.2.0.0")}),-1.0]])]});
            var Q3;
            Q3=makeQuery(id+"F0.imprint","IMPRINT",FACE,{"disambiguationData":[TD([[makeQuery(id+"F0.imprint","IMPRINT",EDGE,{"derivedFrom":sQuery(id+"F0.wireOp",EDGE,"E2.3.0.0")}),-1.0]])]});
            var Q4;
            Q4=makeQuery(id+"F0.imprint","IMPRINT",FACE,{"disambiguationData":[TD([[makeQuery(id+"F0.imprint","IMPRINT",EDGE,{"derivedFrom":sQuery(id+"F0.wireOp",EDGE,"E2.4.0.0")}),-1.0]])]});
            var Q5;
            Q5=makeQuery(id+"F0.imprint","IMPRINT",FACE,{"disambiguationData":[TD([[makeQuery(id+"F0.imprint","IMPRINT",EDGE,{"derivedFrom":sQuery(id+"F0.wireOp",EDGE,"E2.5.0.0")}),-1.0]])]});
            var Q6;
            Q6=makeQuery(id+"F0.imprint","IMPRINT",FACE,{"disambiguationData":[TD([[makeQuery(id+"F0.imprint","IMPRINT",EDGE,{"derivedFrom":sQuery(id+"F0.wireOp",EDGE,"E2.6.0.0")}),-1.0]])]});
            var Q7;
            Q7=makeQuery(id+"F0.imprint","IMPRINT",FACE,{"disambiguationData":[TD([[makeQuery(id+"F0.imprint","IMPRINT",EDGE,{"derivedFrom":sQuery(id+"F0.wireOp",EDGE,"E2.7.0.0")}),-1.0]])]});
            var Q8;
            Q8=makeQuery(id+"F0.imprint","IMPRINT",FACE,{"disambiguationData":[TD([[makeQuery(id+"F0.imprint","IMPRINT",EDGE,{"derivedFrom":sQuery(id+"F0.wireOp",EDGE,"E51.0.1.0")}),1.0]])]});
            var Q9;
            Q9=makeQuery(id+"F0.imprint","IMPRINT",FACE,{"disambiguationData":[TD([[makeQuery(id+"F0.imprint","IMPRINT",EDGE,{"derivedFrom":sQuery(id+"F0.wireOp",EDGE,"E51.0.1.1")}),-1.0]])]});
            var Q10;
            Q10=makeQuery(id+"F0.imprint","IMPRINT",FACE,{"disambiguationData":[TD([[makeQuery(id+"F0.imprint","IMPRINT",EDGE,{"derivedFrom":sQuery(id+"F0.wireOp",EDGE,"E55.0.1.3")}),1.0]])]});
            var Q11;
            Q11=makeQuery(id+"F0.imprint","IMPRINT",FACE,{"disambiguationData":[TD([[makeQuery(id+"F0.imprint","IMPRINT",EDGE,{"derivedFrom":sQuery(id+"F0.wireOp",EDGE,"E55.0.1.0")}),1.0]])]});
            var Q12;
            Q12=makeQuery(id+"F0.imprint","IMPRINT",FACE,{"disambiguationData":[TD([[makeQuery(id+"F0.imprint","IMPRINT",EDGE,{"derivedFrom":sQuery(id+"F0.wireOp",EDGE,"E55.0.2.3")}),1.0]])]});
            var Q13;
            Q13=makeQuery(id+"F0.imprint","IMPRINT",FACE,{"disambiguationData":[TD([[makeQuery(id+"F0.imprint","IMPRINT",EDGE,{"derivedFrom":sQuery(id+"F0.wireOp",EDGE,"E55.0.2.0")}),1.0]])]});
            var Q14;
            Q14=makeQuery(id+"F0.imprint","IMPRINT",FACE,{"disambiguationData":[TD([[makeQuery(id+"F0.imprint","IMPRINT",EDGE,{"derivedFrom":sQuery(id+"F0.wireOp",EDGE,"E62.bottom")}),-1.0]])]});
            var Q15;
            Q15=makeQuery(id+"F0.imprint","IMPRINT",FACE,{"disambiguationData":[TD([[makeQuery(id+"F0.imprint","IMPRINT",EDGE,{"derivedFrom":sQuery(id+"F0.wireOp",EDGE,"E55.0.3.3")}),1.0]])]});
            var Q16;
            Q16=makeQuery(id+"F0.imprint","IMPRINT",FACE,{"disambiguationData":[TD([[makeQuery(id+"F0.imprint","IMPRINT",EDGE,{"derivedFrom":sQuery(id+"F0.wireOp",EDGE,"E55.0.3.0")}),1.0]])]});
            var Q17;
            Q17=makeQuery(id+"F0.imprint","IMPRINT",FACE,{"disambiguationData":[TD([[makeQuery(id+"F0.imprint","IMPRINT",EDGE,{"derivedFrom":sQuery(id+"F0.wireOp",EDGE,"E56.1.0.0")}),1.0]])]});
            var Q18;
            Q18=makeQuery(id+"F0.imprint","IMPRINT",FACE,{"disambiguationData":[TD([[makeQuery(id+"F0.imprint","IMPRINT",EDGE,{"derivedFrom":sQuery(id+"F0.wireOp",EDGE,"E56.1.0.1")}),1.0]])]});
            var Q19;
            Q19=makeQuery(id+"F0.imprint","IMPRINT",FACE,{"disambiguationData":[TD([[makeQuery(id+"F0.imprint","IMPRINT",EDGE,{"derivedFrom":sQuery(id+"F0.wireOp",EDGE,"E61.0.1.4")}),1.0]])]});
            var Q20;
            Q20=makeQuery(id+"F0.imprint","IMPRINT",FACE,{"disambiguationData":[TD([[makeQuery(id+"F0.imprint","IMPRINT",EDGE,{"derivedFrom":sQuery(id+"F0.wireOp",EDGE,"E61.0.1.0")}),1.0]])]});
            var Q21;
            Q21=makeQuery(id+"F0.imprint","IMPRINT",FACE,{"disambiguationData":[TD([[makeQuery(id+"F0.imprint","IMPRINT",EDGE,{"derivedFrom":sQuery(id+"F0.wireOp",EDGE,"E61.0.1.3")}),1.0]])]});
            var Q22;
            Q22=makeQuery(id+"F0.imprint","IMPRINT",FACE,{"disambiguationData":[TD([[makeQuery(id+"F0.imprint","IMPRINT",EDGE,{"derivedFrom":sQuery(id+"F0.wireOp",EDGE,"E61.0.1.1")}),-1.0]])]});
            var Q23;
            Q23=makeQuery(id+"F0.imprint","IMPRINT",FACE,{"disambiguationData":[TD([[makeQuery(id+"F0.imprint","IMPRINT",EDGE,{"derivedFrom":sQuery(id+"F0.wireOp",EDGE,"E61.0.1.5")}),-1.0]])]});
            var Q24;
            Q24=makeQuery(id+"F0.imprint","IMPRINT",FACE,{"disambiguationData":[TD([[makeQuery(id+"F0.imprint","IMPRINT",EDGE,{"derivedFrom":sQuery(id+"F0.wireOp",EDGE,"E60.0.2.9")}),1.0]])]});
            var Q25;
            Q25=makeQuery(id+"F0.imprint","IMPRINT",FACE,{"disambiguationData":[TD([[makeQuery(id+"F0.imprint","IMPRINT",EDGE,{"derivedFrom":sQuery(id+"F0.wireOp",EDGE,"E60.0.2.8")}),1.0]])]});
            var Q26;
            Q26=makeQuery(id+"F0.imprint","IMPRINT",FACE,{"disambiguationData":[TD([[makeQuery(id+"F0.imprint","IMPRINT",EDGE,{"derivedFrom":sQuery(id+"F0.wireOp",EDGE,"E60.0.2.2")}),1.0]])]});
            var Q27;
            Q27=makeQuery(id+"F0.imprint","IMPRINT",FACE,{"disambiguationData":[TD([[makeQuery(id+"F0.imprint","IMPRINT",EDGE,{"derivedFrom":sQuery(id+"F0.wireOp",EDGE,"E60.0.2.1")}),1.0]])]});
            var Q28;
            Q28=makeQuery(id+"F0.imprint","IMPRINT",FACE,{"disambiguationData":[TD([[makeQuery(id+"F0.imprint","IMPRINT",EDGE,{"derivedFrom":sQuery(id+"F0.wireOp",EDGE,"E60.0.2.11")}),1.0]])]});
            var Q29;
            Q29=makeQuery(id+"F0.imprint","IMPRINT",FACE,{"disambiguationData":[TD([[makeQuery(id+"F0.imprint","IMPRINT",EDGE,{"derivedFrom":sQuery(id+"F0.wireOp",EDGE,"E60.0.2.0")}),1.0]])]});
            var Q30;
            Q30=makeQuery(id+"F0.imprint","IMPRINT",FACE,{"disambiguationData":[TD([[makeQuery(id+"F0.imprint","IMPRINT",EDGE,{"derivedFrom":sQuery(id+"F0.wireOp",EDGE,"E60.0.1.0")}),1.0]])]});
            var Q31;
            Q31=makeQuery(id+"F0.imprint","IMPRINT",FACE,{"disambiguationData":[TD([[makeQuery(id+"F0.imprint","IMPRINT",EDGE,{"derivedFrom":sQuery(id+"F0.wireOp",EDGE,"E60.0.1.11")}),1.0]])]});
            var Q32;
            Q32=makeQuery(id+"F0.imprint","IMPRINT",FACE,{"disambiguationData":[TD([[makeQuery(id+"F0.imprint","IMPRINT",EDGE,{"derivedFrom":sQuery(id+"F0.wireOp",EDGE,"E60.0.1.1")}),1.0]])]});
            var Q33;
            Q33=makeQuery(id+"F0.imprint","IMPRINT",FACE,{"disambiguationData":[TD([[makeQuery(id+"F0.imprint","IMPRINT",EDGE,{"derivedFrom":sQuery(id+"F0.wireOp",EDGE,"E60.0.1.2")}),1.0]])]});
            var Q34;
            Q34=makeQuery(id+"F0.imprint","IMPRINT",FACE,{"disambiguationData":[TD([[makeQuery(id+"F0.imprint","IMPRINT",EDGE,{"derivedFrom":sQuery(id+"F0.wireOp",EDGE,"E60.0.1.8")}),1.0]])]});
            var Q35;
            Q35=makeQuery(id+"F0.imprint","IMPRINT",FACE,{"disambiguationData":[TD([[makeQuery(id+"F0.imprint","IMPRINT",EDGE,{"derivedFrom":sQuery(id+"F0.wireOp",EDGE,"E60.0.1.9")}),1.0]])]});
            var Q36;
            Q36=makeQuery(id+"F0.imprint","IMPRINT",FACE,{"disambiguationData":[TD([[makeQuery(id+"F0.imprint","IMPRINT",EDGE,{"derivedFrom":sQuery(id+"F0.wireOp",EDGE,"E59.7.0.0")}),1.0]])]});
            var Q37;
            Q37=makeQuery(id+"F0.imprint","IMPRINT",FACE,{"disambiguationData":[TD([[makeQuery(id+"F0.imprint","IMPRINT",EDGE,{"derivedFrom":sQuery(id+"F0.wireOp",EDGE,"E59.6.0.0")}),1.0]])]});
            var Q38;
            Q38=makeQuery(id+"F0.imprint","IMPRINT",FACE,{"disambiguationData":[TD([[makeQuery(id+"F0.imprint","IMPRINT",EDGE,{"derivedFrom":sQuery(id+"F0.wireOp",EDGE,"E59.5.0.0")}),1.0]])]});
            var Q39;
            Q39=makeQuery(id+"F0.imprint","IMPRINT",FACE,{"disambiguationData":[TD([[makeQuery(id+"F0.imprint","IMPRINT",EDGE,{"derivedFrom":sQuery(id+"F0.wireOp",EDGE,"E59.4.0.0")}),1.0]])]});
            var Q40;
            Q40=makeQuery(id+"F0.imprint","IMPRINT",FACE,{"disambiguationData":[TD([[makeQuery(id+"F0.imprint","IMPRINT",EDGE,{"derivedFrom":sQuery(id+"F0.wireOp",EDGE,"E59.3.0.0")}),1.0]])]});
            var Q41;
            Q41=makeQuery(id+"F0.imprint","IMPRINT",FACE,{"disambiguationData":[TD([[makeQuery(id+"F0.imprint","IMPRINT",EDGE,{"derivedFrom":sQuery(id+"F0.wireOp",EDGE,"E59.2.0.0")}),1.0]])]});
            var Q42;
            Q42=makeQuery(id+"F0.imprint","IMPRINT",FACE,{"disambiguationData":[TD([[makeQuery(id+"F0.imprint","IMPRINT",EDGE,{"derivedFrom":sQuery(id+"F0.wireOp",EDGE,"E59.1.0.0")}),1.0]])]});
            var Q43;
            Q43=makeQuery(id+"F0.imprint","IMPRINT",FACE,{"disambiguationData":[TD([[makeQuery(id+"F0.imprint","IMPRINT",EDGE,{"derivedFrom":sQuery(id+"F0.wireOp",EDGE,"E58.1.0.0")}),-1.0]])]});
            extrude(context, id + "F2", {"entities" : qUnion([Q0, Q1, Q2, Q3, Q4, Q5, Q6, Q7, Q8, Q9, Q10, Q11, Q12, Q13, Q14, Q15, Q16, Q17, Q18, Q19, Q20, Q21, Q22, Q23, Q24, Q25, Q26, Q27, Q28, Q29, Q30, Q31, Q32, Q33, Q34, Q35, Q36, Q37, Q38, Q39, Q40, Q41, Q42, Q43]), "operationType" : NewBodyOperationType.ADD, "depth" : 82 * mm, "offsetDistance" : 25 * mm});
        }
        {
            var Q0;
            Q0=makeQuery(id+"F0.imprint","IMPRINT",FACE,{"disambiguationData":[TD([[makeQuery(id+"F0.imprint","IMPRINT",EDGE,{"derivedFrom":sQuery(id+"F0.wireOp",EDGE,"E53.bottom")}),-1.0]])]});
            var Q1;
            Q1=makeQuery(id+"F0.imprint","IMPRINT",FACE,{"disambiguationData":[TD([[makeQuery(id+"F0.imprint","IMPRINT",EDGE,{"derivedFrom":sQuery(id+"F0.wireOp",EDGE,"E52.bottom")}),-1.0]])]});
            var Q2;
            Q2=makeQuery(id+"F0.imprint","IMPRINT",FACE,{"disambiguationData":[TD([[makeQuery(id+"F0.imprint","IMPRINT",EDGE,{"derivedFrom":sQuery(id+"F0.wireOp",EDGE,"E54.bottom")}),-1.0]])]});
            var Q3;
            Q3=makeQuery(id+"F0.imprint","IMPRINT",FACE,{"disambiguationData":[TD([[makeQuery(id+"F0.imprint","IMPRINT",EDGE,{"derivedFrom":sQuery(id+"F0.wireOp",EDGE,"E57.bottom")}),-1.0]])]});
            extrude(context, id + "F3", {"entities" : qUnion([Q0, Q1, Q2, Q3]), "operationType" : NewBodyOperationType.ADD, "depth" : 191 * mm, "offsetDistance" : 25 * mm});
        }
    });
